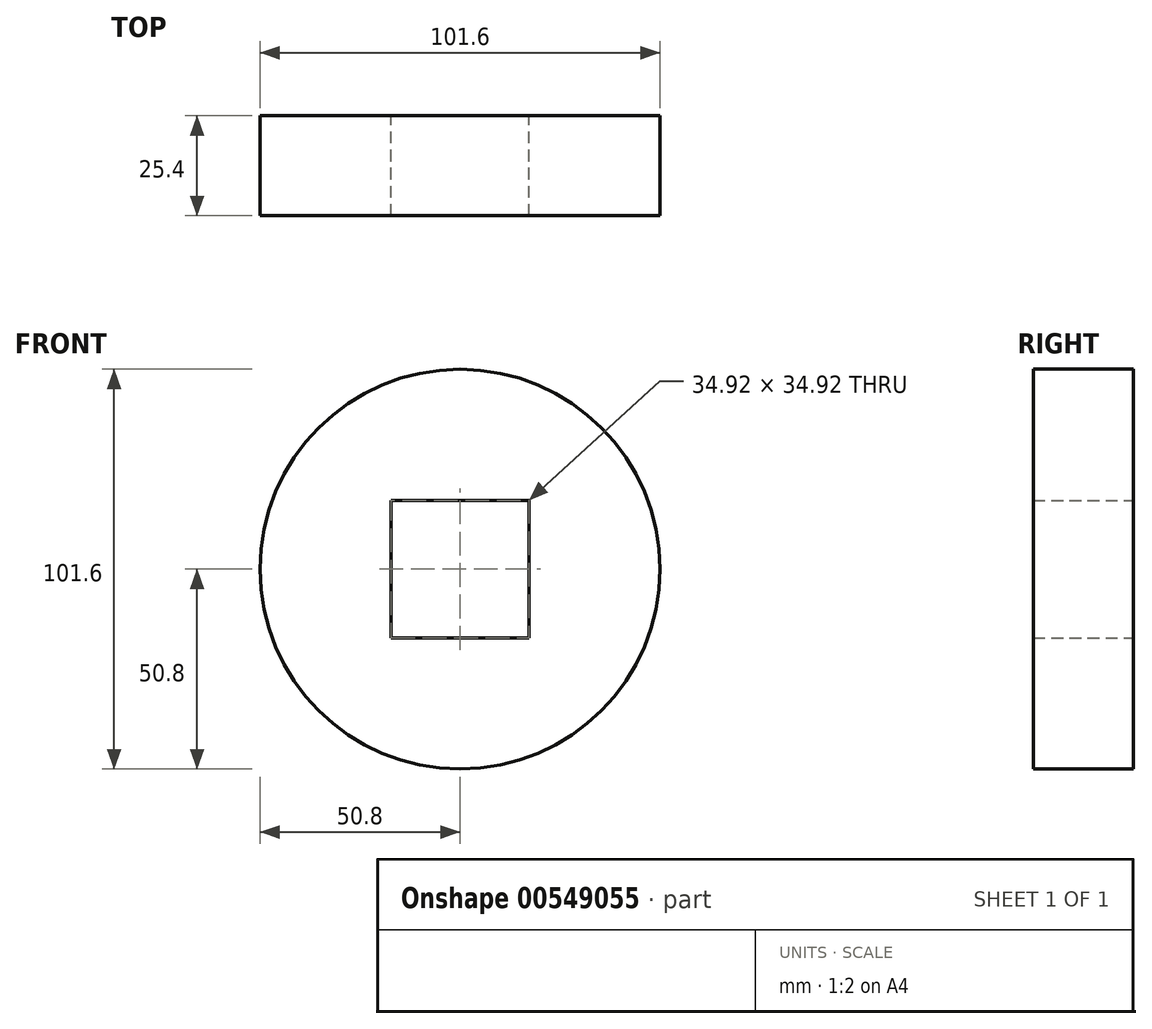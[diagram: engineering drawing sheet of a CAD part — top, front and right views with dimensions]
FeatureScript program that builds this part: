
annotation { "Feature Type Name" : "Feature", "Feature Type Description" : "" }
export const myFeature = defineFeature(function(context is Context, id is Id, definition is map)
    precondition{}
    {
        {
            var Q0;
            Q0=qCreatedBy(makeId("Front.planeOp"),FACE);
            var sketch = newSketch(context, id + "F0", { "sketchPlane" : qUnion([Q0])});
            skCircle(sketch, "E0", {"center": v(0, 0) * mm, "radius": 50.8 * mm});
            skLineSegment(sketch, "E1.bottom", {"start": v(17.46, 17.46) * mm, "end": v(-17.46, 17.46) * mm});
            skLineSegment(sketch, "E1.top", {"start": v(17.46, -17.46) * mm, "end": v(-17.46, -17.46) * mm});
            skLineSegment(sketch, "E1.left", {"start": v(17.46, 17.46) * mm, "end": v(17.46, -17.46) * mm});
            skLineSegment(sketch, "E1.right", {"start": v(-17.46, 17.46) * mm, "end": v(-17.46, -17.46) * mm});
            skSolve(sketch);
        }
        {
            var Q0;
            Q0=makeQuery(id+"F0.imprint","IMPRINT",FACE,{"disambiguationData":[TD([[makeQuery(id+"F0.imprint","IMPRINT",EDGE,{"derivedFrom":sQuery(id+"F0.wireOp",EDGE,"E0")}),1.0]])]});
            extrude(context, id + "F1", {"entities" : qUnion([Q0]), "depth" : 25.4 * mm, "offsetDistance" : 25.4 * mm});
        }
    });
